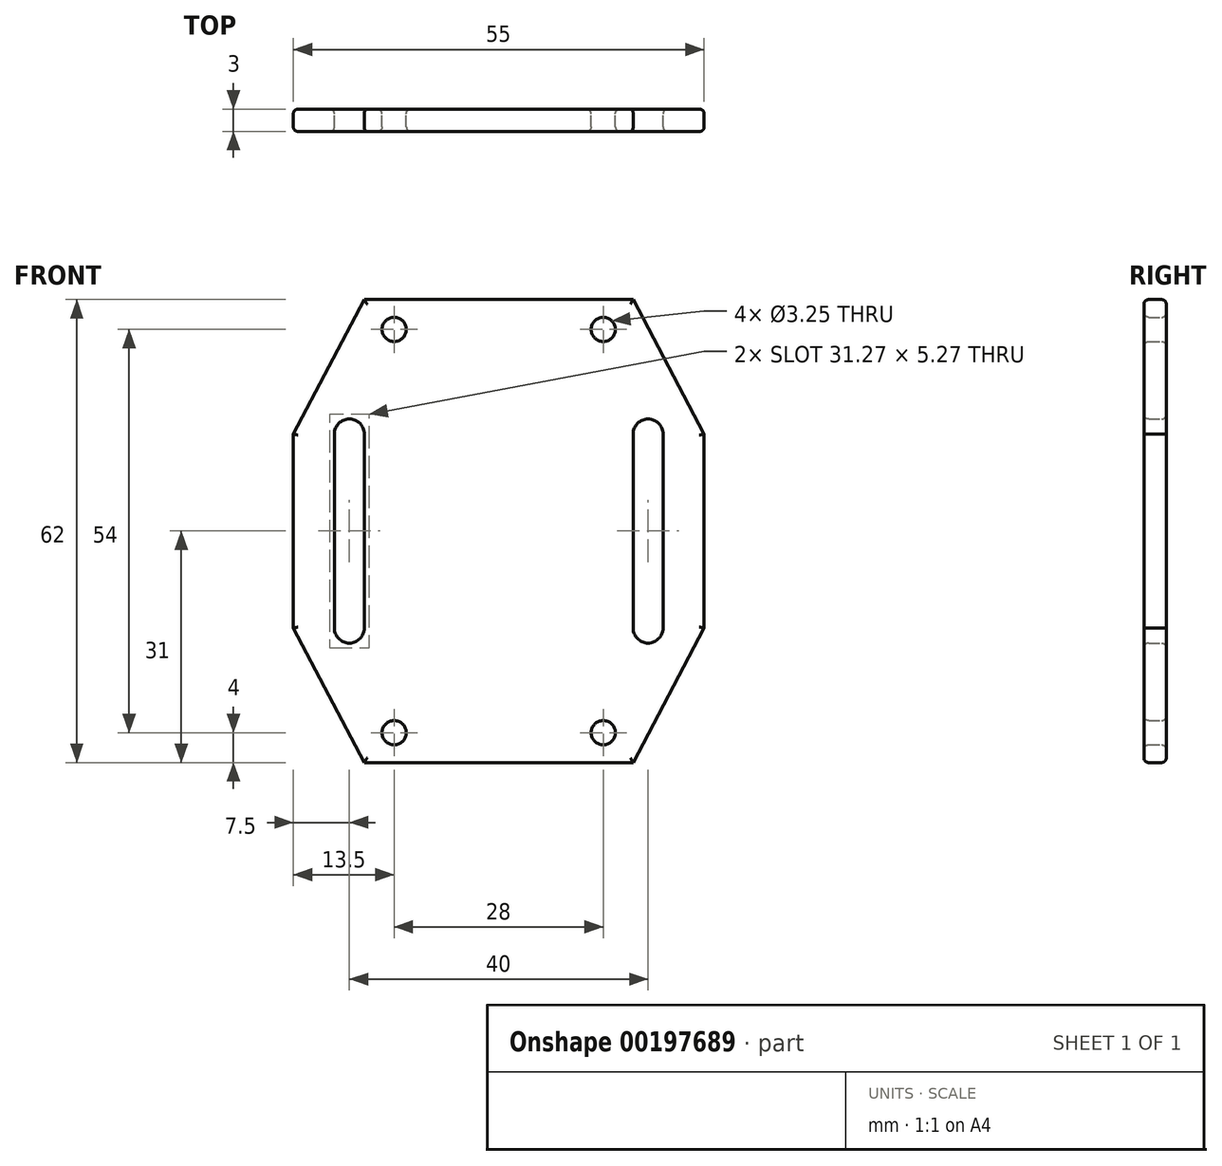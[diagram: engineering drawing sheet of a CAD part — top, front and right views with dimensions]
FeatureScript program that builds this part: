
annotation { "Feature Type Name" : "Feature", "Feature Type Description" : "" }
export const myFeature = defineFeature(function(context is Context, id is Id, definition is map)
    precondition{}
    {
        {
            var Q0;
            Q0=qCreatedBy(makeId("Front.planeOp"),FACE);
            var sketch = newSketch(context, id + "F0", { "sketchPlane" : qUnion([Q0])});
            skLineSegment(sketch, "E0.bottom", {"start": v(14, 27) * mm, "end": v(-14, 27) * mm, "construction": true});
            skLineSegment(sketch, "E0.top", {"start": v(14, -27) * mm, "end": v(-14, -27) * mm, "construction": true});
            skLineSegment(sketch, "E0.left", {"start": v(14, 27) * mm, "end": v(14, -27) * mm, "construction": true});
            skLineSegment(sketch, "E0.right", {"start": v(-14, 27) * mm, "end": v(-14, -27) * mm, "construction": true});
            skPoint(sketch, "E0.middle", {"position": v(0, 0) * mm});
            skCircle(sketch, "E1", {"center": v(-14, 27) * mm, "radius": 1.63 * mm});
            skCircle(sketch, "E2", {"center": v(14, 27) * mm, "radius": 1.63 * mm});
            skCircle(sketch, "E3", {"center": v(14, -27) * mm, "radius": 1.63 * mm});
            skCircle(sketch, "E4", {"center": v(-14, -27) * mm, "radius": 1.63 * mm});
            skLineSegment(sketch, "E5.bottom", {"start": v(-18, 31) * mm, "end": v(18, 31) * mm});
            skLineSegment(sketch, "E5.top", {"start": v(-18, -31) * mm, "end": v(18, -31) * mm});
            skLineSegment(sketch, "E5.left", {"start": v(-27.5, 13) * mm, "end": v(-27.5, -13) * mm});
            skLineSegment(sketch, "E5.right", {"start": v(27.5, 13) * mm, "end": v(27.5, -13) * mm});
            skLineSegment(sketch, "E6", {"start": v(-18, 31) * mm, "end": v(-27.5, 13) * mm});
            skLineSegment(sketch, "E7", {"start": v(0, 31) * mm, "end": v(0, -31) * mm, "construction": true});
            skLineSegment(sketch, "E8", {"start": v(-27.5, 0) * mm, "end": v(27.5, 0) * mm, "construction": true});
            skLineSegment(sketch, "E9.MirrorCS", {"start": v(18, 31) * mm, "end": v(27.5, 13) * mm});
            skLineSegment(sketch, "E10.MirrorCS", {"start": v(18, -31) * mm, "end": v(27.5, -13) * mm});
            skLineSegment(sketch, "E11.MirrorCS", {"start": v(-18, -31) * mm, "end": v(-27.5, -13) * mm});
            skPoint(sketch, "E12.orphan", {"position": v(27.5, 31) * mm});
            skPoint(sketch, "E13.orphan", {"position": v(27.5, -31) * mm});
            skPoint(sketch, "E14.orphan", {"position": v(-27.5, -31) * mm});
            skPoint(sketch, "E15.orphan", {"position": v(-27.5, 31) * mm});
            skLineSegment(sketch, "E16", {"start": v(20, 13) * mm, "end": v(20, -13) * mm, "construction": true});
            skLineSegment(sketch, "E17", {"start": v(22, 13) * mm, "end": v(22, -13) * mm});
            skLineSegment(sketch, "E18", {"start": v(18, 13) * mm, "end": v(18, -13) * mm});
            skArc(sketch, "E19", {"start": v(22, 13) * mm, "mid": v(20, 15) * mm, "end": v(18, 13) * mm});
            skArc(sketch, "E20", {"start": v(18, -13) * mm, "mid": v(20, -15) * mm, "end": v(22, -13) * mm});
            skLineSegment(sketch, "E21.MirrorCS", {"start": v(-20, 13) * mm, "end": v(-20, -13) * mm, "construction": true});
            skArc(sketch, "E22.MirrorCS", {"start": v(-22, 13) * mm, "mid": v(-20, 15) * mm, "end": v(-18, 13) * mm});
            skLineSegment(sketch, "E23.MirrorCS", {"start": v(-18, 13) * mm, "end": v(-18, -13) * mm});
            skLineSegment(sketch, "E24.MirrorCS", {"start": v(-22, 13) * mm, "end": v(-22, -13) * mm});
            skArc(sketch, "E25.MirrorCS", {"start": v(-18, -13) * mm, "mid": v(-20, -15) * mm, "end": v(-22, -13) * mm});
            skSolve(sketch);
        }
        {
            var Q0;
            Q0 = qSketchRegion(id + "F0", true);
            extrude(context, id + "F1", {"entities" : qUnion([Q0]), "depth" : 3 * mm});
        }
        {
            var Q0;
            Q0=makeQuery(id+"F1.opExtrude","CAP_FACE",FACE,{"disambiguationData":[OSD([sQuery(id+"F0.wireOp",EDGE,"E1"),sQuery(id+"F0.wireOp",EDGE,"E2"),sQuery(id+"F0.wireOp",EDGE,"E3"),sQuery(id+"F0.wireOp",EDGE,"E4"),sQuery(id+"F0.wireOp",EDGE,"E5.bottom"),sQuery(id+"F0.wireOp",EDGE,"E5.top"),sQuery(id+"F0.wireOp",EDGE,"E5.left"),sQuery(id+"F0.wireOp",EDGE,"E5.right"),sQuery(id+"F0.wireOp",EDGE,"E6"),sQuery(id+"F0.wireOp",EDGE,"E9.MirrorCS"),sQuery(id+"F0.wireOp",EDGE,"E10.MirrorCS"),sQuery(id+"F0.wireOp",EDGE,"E11.MirrorCS"),sQuery(id+"F0.wireOp",EDGE,"E17"),sQuery(id+"F0.wireOp",EDGE,"E18"),sQuery(id+"F0.wireOp",EDGE,"E19"),sQuery(id+"F0.wireOp",EDGE,"E20"),sQuery(id+"F0.wireOp",EDGE,"E22.MirrorCS"),sQuery(id+"F0.wireOp",EDGE,"E23.MirrorCS"),sQuery(id+"F0.wireOp",EDGE,"E24.MirrorCS"),sQuery(id+"F0.wireOp",EDGE,"E25.MirrorCS")])],"isStart":false});
            fillet(context, id + "F2", {"entities" : qUnion([Q0]), "radius" : 0.64 * mm, "tangentPropagation" : true, "allowEdgeOverflow" : false});
        }
        {
            var Q0;
            Q0=makeQuery(id+"F1.opExtrude","CAP_FACE",FACE,{"disambiguationData":[OSD([sQuery(id+"F0.wireOp",EDGE,"E1"),sQuery(id+"F0.wireOp",EDGE,"E2"),sQuery(id+"F0.wireOp",EDGE,"E3"),sQuery(id+"F0.wireOp",EDGE,"E4"),sQuery(id+"F0.wireOp",EDGE,"E5.bottom"),sQuery(id+"F0.wireOp",EDGE,"E5.top"),sQuery(id+"F0.wireOp",EDGE,"E5.left"),sQuery(id+"F0.wireOp",EDGE,"E5.right"),sQuery(id+"F0.wireOp",EDGE,"E6"),sQuery(id+"F0.wireOp",EDGE,"E9.MirrorCS"),sQuery(id+"F0.wireOp",EDGE,"E10.MirrorCS"),sQuery(id+"F0.wireOp",EDGE,"E11.MirrorCS"),sQuery(id+"F0.wireOp",EDGE,"E17"),sQuery(id+"F0.wireOp",EDGE,"E18"),sQuery(id+"F0.wireOp",EDGE,"E19"),sQuery(id+"F0.wireOp",EDGE,"E20"),sQuery(id+"F0.wireOp",EDGE,"E22.MirrorCS"),sQuery(id+"F0.wireOp",EDGE,"E23.MirrorCS"),sQuery(id+"F0.wireOp",EDGE,"E24.MirrorCS"),sQuery(id+"F0.wireOp",EDGE,"E25.MirrorCS")])],"isStart":true});
            fillet(context, id + "F3", {"entities" : qUnion([Q0]), "radius" : 0.64 * mm, "tangentPropagation" : true, "allowEdgeOverflow" : false});
        }
    });
